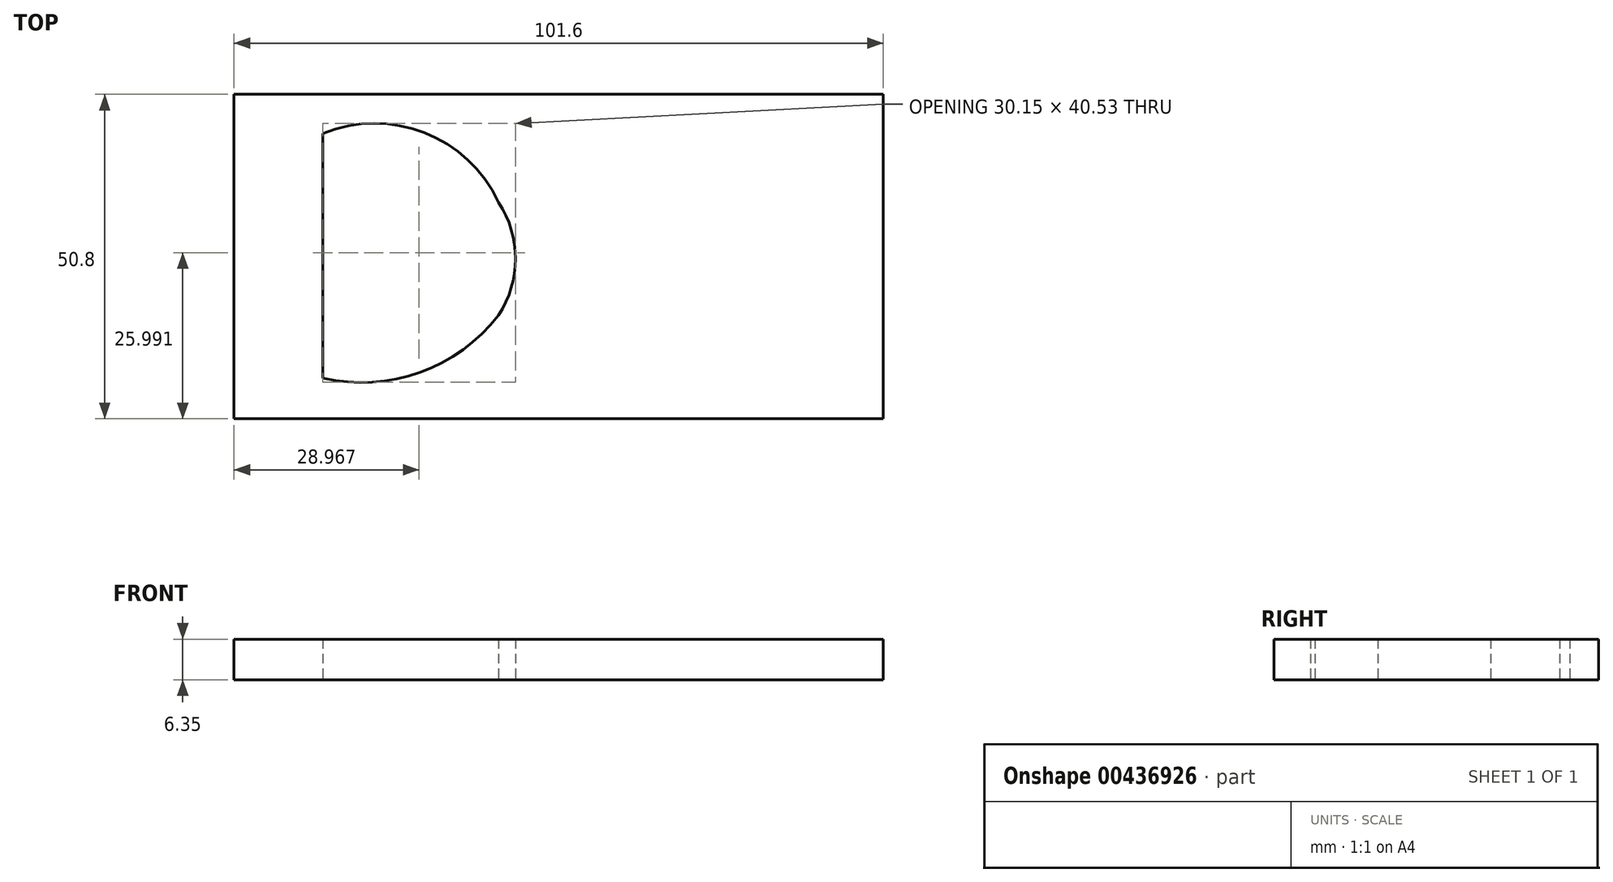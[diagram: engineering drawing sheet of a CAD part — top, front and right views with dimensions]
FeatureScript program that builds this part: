
annotation { "Feature Type Name" : "Feature", "Feature Type Description" : "" }
export const myFeature = defineFeature(function(context is Context, id is Id, definition is map)
    precondition{}
    {
        {
            var Q0;
            Q0=qCreatedBy(makeId("Top.planeOp"),FACE);
            var sketch = newSketch(context, id + "F0", { "sketchPlane" : qUnion([Q0])});
            skLineSegment(sketch, "E0.bottom", {"start": v(-50.8, -25.4) * mm, "end": v(50.8, -25.4) * mm});
            skLineSegment(sketch, "E0.top", {"start": v(-50.8, 25.4) * mm, "end": v(50.8, 25.4) * mm});
            skLineSegment(sketch, "E0.left", {"start": v(-50.8, -25.4) * mm, "end": v(-50.8, 25.4) * mm});
            skLineSegment(sketch, "E0.right", {"start": v(50.8, -25.4) * mm, "end": v(50.8, 25.4) * mm});
            skPoint(sketch, "E0.middle", {"position": v(0, 0) * mm});
            skLineSegment(sketch, "E1", {"start": v(-36.91, 19.26) * mm, "end": v(-36.91, -19.03) * mm});
            skArc(sketch, "E2", {"start": v(-9.4, 8.48) * mm, "mid": v(-21, 19.39) * mm, "end": v(-36.91, 19.26) * mm});
            skArc(sketch, "E3", {"start": v(-9.4, -9.17) * mm, "mid": v(-6.76, -0.34) * mm, "end": v(-9.4, 8.48) * mm});
            skArc(sketch, "E4", {"start": v(-36.91, -19.03) * mm, "mid": v(-21.7, -18.14) * mm, "end": v(-9.4, -9.17) * mm});
            skSolve(sketch);
        }
        {
            var Q0;
            Q0=makeQuery(id+"F0.imprint","IMPRINT",FACE,{"disambiguationData":[TD([[makeQuery(id+"F0.imprint","IMPRINT",EDGE,{"derivedFrom":sQuery(id+"F0.wireOp",EDGE,"E0.bottom")}),1.0]])]});
            extrude(context, id + "F1", {"entities" : qUnion([Q0]), "depth" : 6.35 * mm});
        }
    });
